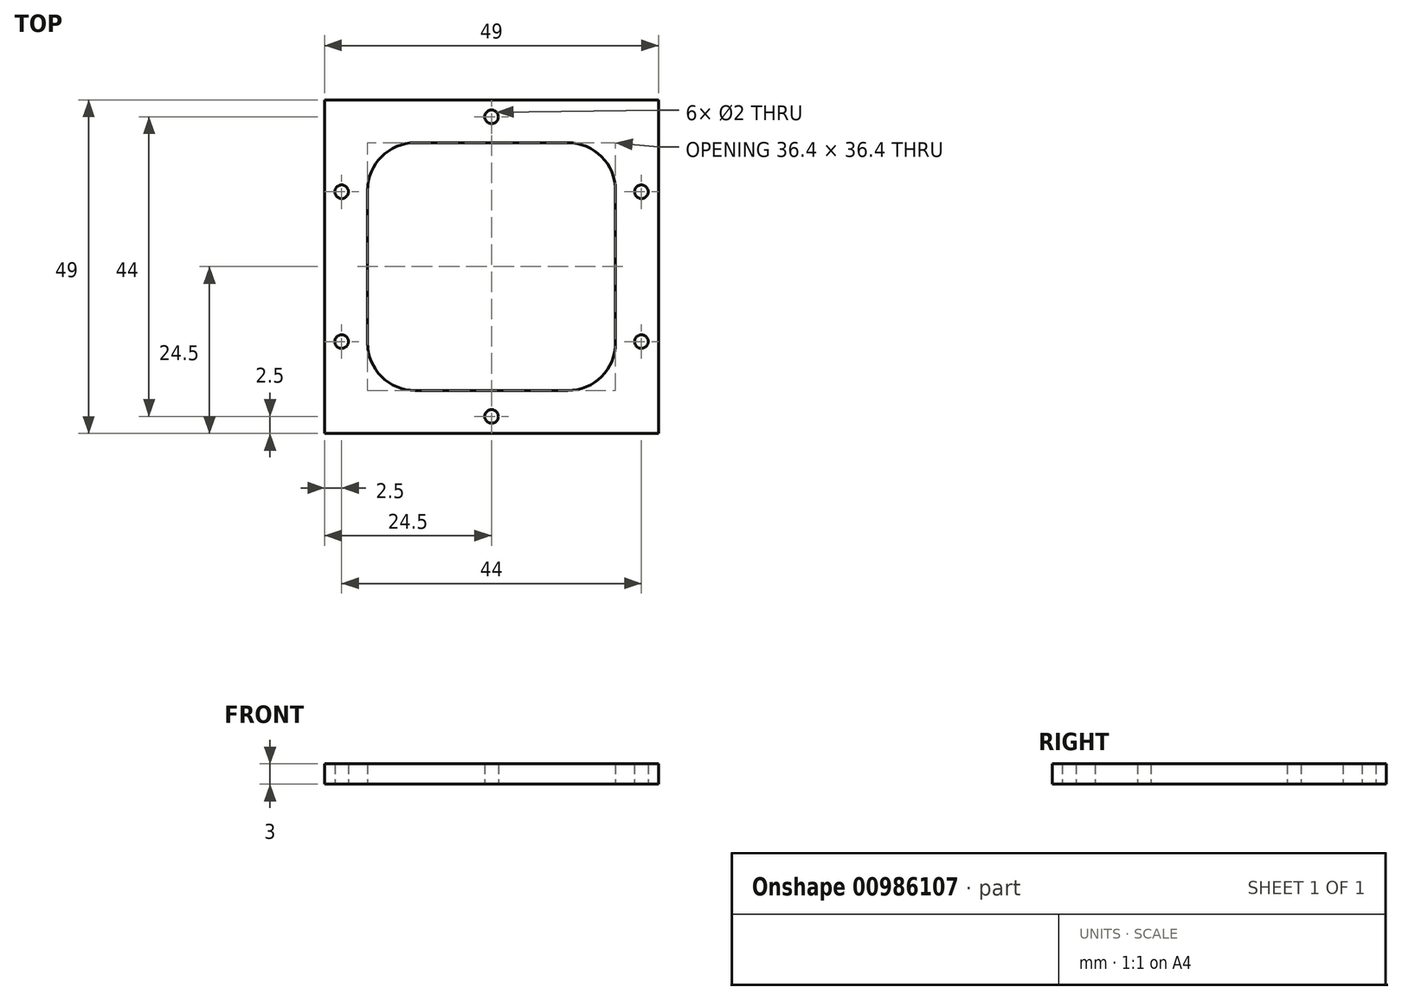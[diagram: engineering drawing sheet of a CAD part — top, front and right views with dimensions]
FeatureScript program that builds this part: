
annotation { "Feature Type Name" : "Feature", "Feature Type Description" : "" }
export const myFeature = defineFeature(function(context is Context, id is Id, definition is map)
    precondition{}
    {
        {
            var Q0;
            Q0=qCreatedBy(makeId("Top.planeOp"),FACE);
            var sketch = newSketch(context, id + "F0", { "sketchPlane" : qUnion([Q0])});
            skLineSegment(sketch, "E0.bottom", {"start": v(18.2, 18.2) * mm, "end": v(-18.2, 18.2) * mm});
            skLineSegment(sketch, "E0.top", {"start": v(18.2, -18.2) * mm, "end": v(-18.2, -18.2) * mm});
            skLineSegment(sketch, "E0.left", {"start": v(18.2, 18.2) * mm, "end": v(18.2, -18.2) * mm});
            skLineSegment(sketch, "E0.right", {"start": v(-18.2, 18.2) * mm, "end": v(-18.2, -18.2) * mm});
            skPoint(sketch, "E0.middle", {"position": v(0, 0) * mm});
            skLineSegment(sketch, "E1.bottom", {"start": v(19.5, 19.5) * mm, "end": v(-19.5, 19.5) * mm});
            skLineSegment(sketch, "E1.right", {"start": v(-19.5, 19.5) * mm, "end": v(-19.5, -19.5) * mm});
            skLineSegment(sketch, "E2", {"start": v(-19.5, -19.5) * mm, "end": v(19.5, -19.5) * mm});
            skLineSegment(sketch, "E3", {"start": v(19.5, 19.5) * mm, "end": v(19.5, -19.5) * mm});
            skLineSegment(sketch, "E4", {"start": v(-24.5, -24.5) * mm, "end": v(24.5, -24.5) * mm});
            skLineSegment(sketch, "E5", {"start": v(24.5, -24.5) * mm, "end": v(24.5, 24.5) * mm});
            skLineSegment(sketch, "E6", {"start": v(24.5, 24.5) * mm, "end": v(-24.5, 24.5) * mm});
            skLineSegment(sketch, "E7", {"start": v(-24.5, -24.5) * mm, "end": v(-24.5, 24.5) * mm});
            skCircle(sketch, "E8", {"center": v(0, 22) * mm, "radius": 1 * mm});
            skCircle(sketch, "E9.MirrorC", {"center": v(0, -22) * mm, "radius": 1 * mm});
            skLineSegment(sketch, "E10", {"start": v(-24.5, 24.5) * mm, "end": v(-22, 24.5) * mm});
            skLineSegment(sketch, "E11", {"start": v(-18.2, -18.2) * mm, "end": v(-18.2, -19.5) * mm});
            skCircle(sketch, "E12", {"center": v(-22, -11) * mm, "radius": 1 * mm});
            skCircle(sketch, "E13", {"center": v(-22, 11) * mm, "radius": 1 * mm});
            skCircle(sketch, "E14", {"center": v(22, 11) * mm, "radius": 1 * mm});
            skCircle(sketch, "E15", {"center": v(22, -11) * mm, "radius": 1 * mm});
            skSolve(sketch);
        }
        {
            var Q0;
            Q0=makeQuery(id+"F0.imprint","IMPRINT",FACE,{"disambiguationData":[TD([[makeQuery(id+"F0.imprint","IMPRINT",EDGE,{"derivedFrom":sQuery(id+"F0.wireOp",EDGE,"E0.bottom")}),-1.0]])]});
            var Q1;
            Q1=makeQuery(id+"F0.imprint","IMPRINT",FACE,{"disambiguationData":[TD([[makeQuery(id+"F0.imprint","IMPRINT",EDGE,{"derivedFrom":sQuery(id+"F0.wireOp",EDGE,"E1.bottom")}),-1.0]])]});
            extrude(context, id + "F1", {"entities" : qUnion([Q0, Q1]), "depth" : 3 * mm, "offsetDistance" : 25 * mm});
        }
        {
            var Q0;
            Q0=makeQuery(id+"F1.opExtrude","SWEPT_EDGE",EDGE,{"disambiguationData":[OSD([sQuery(id+"F0.wireOp",EDGE,"E0.bottom"),sQuery(id+"F0.wireOp",EDGE,"E0.right")])]});
            var Q1;
            Q1=makeQuery(id+"F1.opExtrude","SWEPT_EDGE",EDGE,{"disambiguationData":[OSD([sQuery(id+"F0.wireOp",EDGE,"E0.top"),sQuery(id+"F0.wireOp",EDGE,"E0.right")])]});
            var Q2;
            Q2=makeQuery(id+"F1.opExtrude","SWEPT_EDGE",EDGE,{"disambiguationData":[OSD([sQuery(id+"F0.wireOp",EDGE,"E0.top"),sQuery(id+"F0.wireOp",EDGE,"E0.left")])]});
            var Q3;
            Q3=makeQuery(id+"F1.opExtrude","SWEPT_EDGE",EDGE,{"disambiguationData":[OSD([sQuery(id+"F0.wireOp",EDGE,"E0.bottom"),sQuery(id+"F0.wireOp",EDGE,"E0.left")])]});
            fillet(context, id + "F2", {"entities" : qUnion([Q0, Q1, Q2, Q3]), "tangentPropagation" : true, "radius" : 7 * mm, "defaultsChanged" : true, "vertexSettings" : [], "allowEdgeOverflow" : false});
        }
    });
